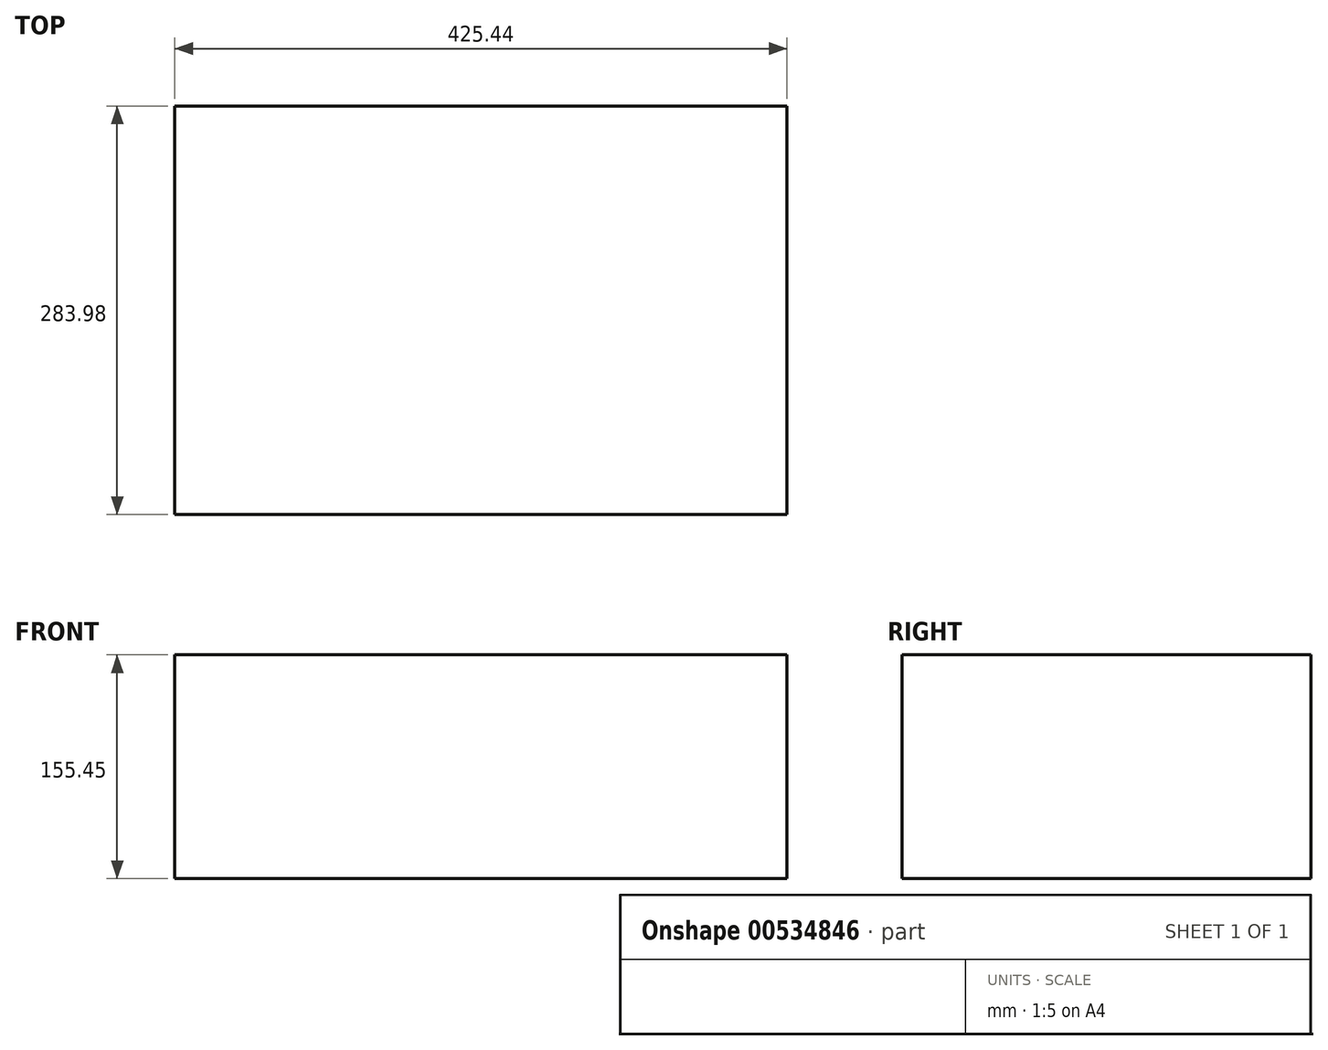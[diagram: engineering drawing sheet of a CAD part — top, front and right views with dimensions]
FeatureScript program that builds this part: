
annotation { "Feature Type Name" : "Feature", "Feature Type Description" : "" }
export const myFeature = defineFeature(function(context is Context, id is Id, definition is map)
    precondition{}
    {
        {
            var Q0;
            Q0=qCreatedBy(makeId("Top.planeOp"),FACE);
            var sketch = newSketch(context, id + "F0", { "sketchPlane" : qUnion([Q0])});
            skLineSegment(sketch, "E0.bottom", {"start": v(212.73, -141.99) * mm, "end": v(-212.73, -141.99) * mm});
            skLineSegment(sketch, "E0.top", {"start": v(212.73, 141.99) * mm, "end": v(-212.73, 141.99) * mm});
            skLineSegment(sketch, "E0.left", {"start": v(212.73, -141.99) * mm, "end": v(212.73, 141.99) * mm});
            skLineSegment(sketch, "E0.right", {"start": v(-212.73, -141.99) * mm, "end": v(-212.73, 141.99) * mm});
            skPoint(sketch, "E0.middle", {"position": v(0, 0) * mm});
            skSolve(sketch);
        }
        {
            var Q0;
            Q0=makeQuery(id+"F0.imprint","IMPRINT",FACE,{"disambiguationData":[TD([[makeQuery(id+"F0.imprint","IMPRINT",EDGE,{"derivedFrom":sQuery(id+"F0.wireOp",EDGE,"E0.bottom")}),-1.0]])]});
            extrude(context, id + "F1", {"entities" : qUnion([Q0]), "depth" : 155.45 * mm, "offsetDistance" : 25 * mm});
        }
    });
